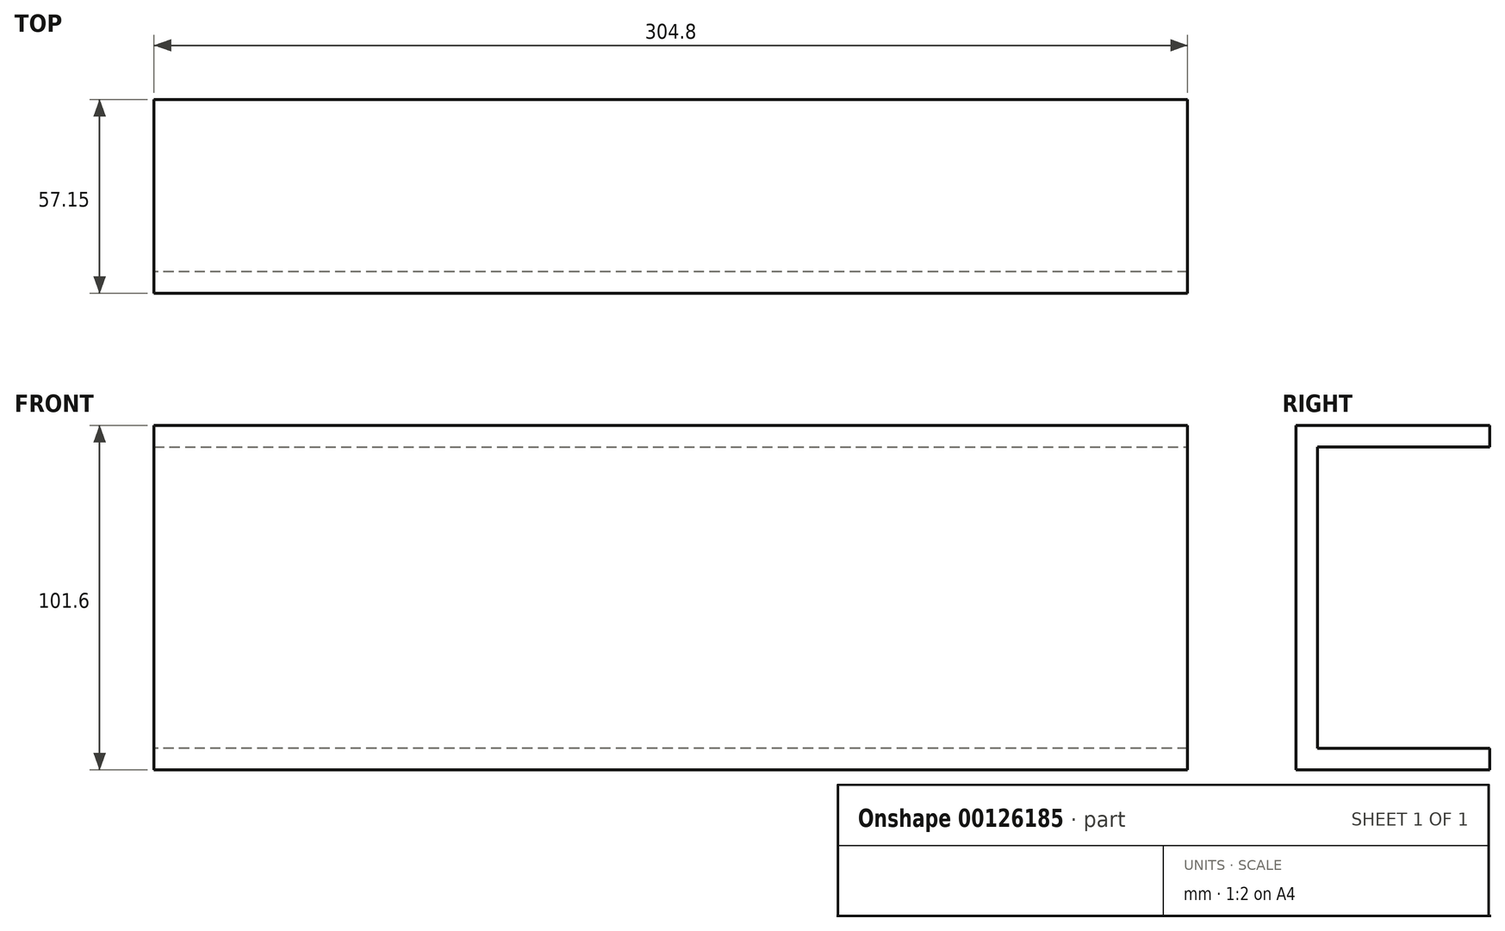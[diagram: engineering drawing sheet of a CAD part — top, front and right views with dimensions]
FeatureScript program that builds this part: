
annotation { "Feature Type Name" : "Feature", "Feature Type Description" : "" }
export const myFeature = defineFeature(function(context is Context, id is Id, definition is map)
    precondition{}
    {
        {
            var Q0;
            Q0=qCreatedBy(makeId("Front.planeOp"),FACE);
            var sketch = newSketch(context, id + "F0", { "sketchPlane" : qUnion([Q0])});
            skLineSegment(sketch, "E0", {"start": v(-132.9, -63.31) * mm, "end": v(171.9, -63.31) * mm});
            skLineSegment(sketch, "E1", {"start": v(-132.9, -63.31) * mm, "end": v(-132.9, 38.29) * mm});
            skLineSegment(sketch, "E2", {"start": v(171.9, 38.29) * mm, "end": v(-132.9, 38.29) * mm});
            skLineSegment(sketch, "E3", {"start": v(171.9, 38.29) * mm, "end": v(171.9, -63.31) * mm});
            skSolve(sketch);
        }
        {
            var Q0;
            Q0=makeQuery(id+"F0.imprint","IMPRINT",FACE,{"disambiguationData":[TD([[makeQuery(id+"F0.imprint","IMPRINT",EDGE,{"derivedFrom":sQuery(id+"F0.wireOp",EDGE,"E0")}),1.0]])]});
            extrude(context, id + "F1", {"entities" : qUnion([Q0]), "depth" : 6.35 * mm});
        }
        {
            var Q0;
            Q0=makeQuery(id+"F1.opExtrude","CAP_FACE",FACE,{"disambiguationData":[OSD([sQuery(id+"F0.wireOp",EDGE,"E0"),sQuery(id+"F0.wireOp",EDGE,"E1"),sQuery(id+"F0.wireOp",EDGE,"E2"),sQuery(id+"F0.wireOp",EDGE,"E3")])],"isStart":true});
            var sketch = newSketch(context, id + "F2", { "sketchPlane" : qUnion([Q0])});
            skLineSegment(sketch, "E4", {"start": v(132.9, 38.29) * mm, "end": v(132.9, 31.94) * mm});
            skLineSegment(sketch, "E5", {"start": v(132.9, 31.94) * mm, "end": v(-171.9, 31.94) * mm});
            skLineSegment(sketch, "E6", {"start": v(-171.9, 31.94) * mm, "end": v(-171.9, 38.29) * mm});
            skLineSegment(sketch, "E7", {"start": v(-171.9, -63.31) * mm, "end": v(-171.9, -56.96) * mm});
            skLineSegment(sketch, "E8", {"start": v(-171.9, -56.96) * mm, "end": v(132.9, -56.96) * mm});
            skLineSegment(sketch, "E9", {"start": v(132.9, -56.96) * mm, "end": v(132.9, -63.31) * mm});
            skLineSegment(sketch, "E10", {"start": v(132.9, -63.31) * mm, "end": v(-171.9, -63.31) * mm});
            skSolve(sketch);
        }
        {
            var Q0;
            Q0=makeQuery(id+"F2.imprint","IMPRINT",FACE,{"disambiguationData":[TD([[makeQuery(id+"F2.imprint","IMPRINT",EDGE,{"derivedFrom":sQuery(id+"F2.wireOp",EDGE,"E4")}),1.0]])]});
            extrude(context, id + "F3", {"entities" : qUnion([Q0]), "operationType" : NewBodyOperationType.ADD, "depth" : 50.8 * mm});
        }
        {
            var Q0;
            Q0=makeQuery(id+"F2.imprint","IMPRINT",FACE,{"disambiguationData":[TD([[makeQuery(id+"F2.imprint","IMPRINT",EDGE,{"derivedFrom":sQuery(id+"F2.wireOp",EDGE,"E7")}),1.0]])]});
            extrude(context, id + "F4", {"entities" : qUnion([Q0]), "operationType" : NewBodyOperationType.ADD, "depth" : 50.8 * mm});
        }
    });
